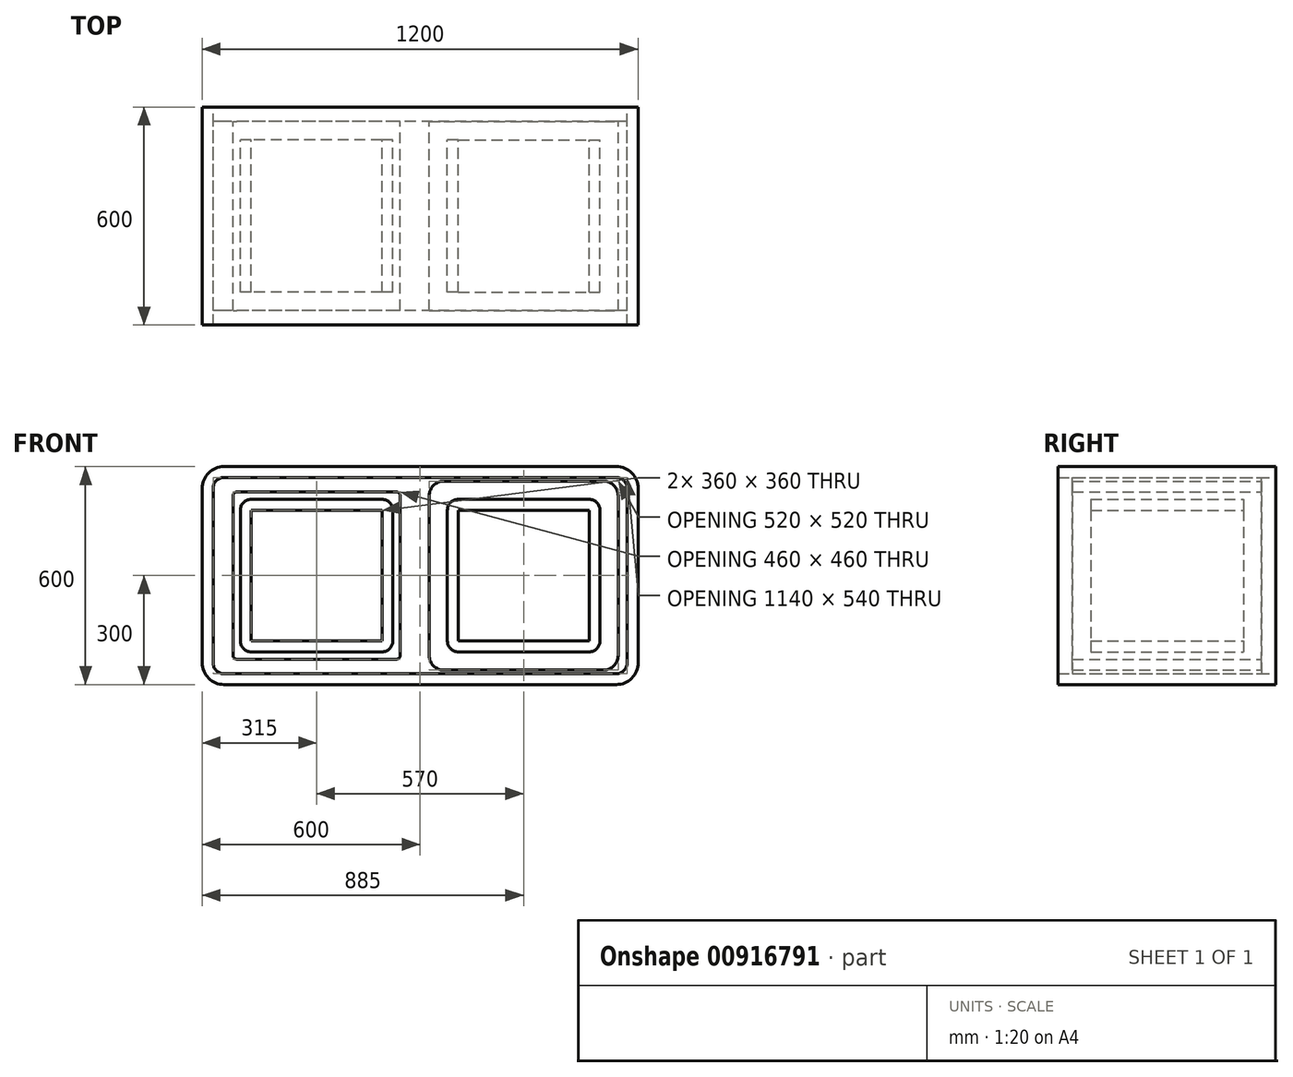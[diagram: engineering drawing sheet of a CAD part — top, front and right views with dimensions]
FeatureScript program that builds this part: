
annotation { "Feature Type Name" : "Feature", "Feature Type Description" : "" }
export const myFeature = defineFeature(function(context is Context, id is Id, definition is map)
    precondition{}
    {
        {
            var Q0;
            Q0=qCreatedBy(makeId("Front.planeOp"),FACE);
            var sketch = newSketch(context, id + "F0", { "sketchPlane" : qUnion([Q0])});
            skLineSegment(sketch, "E0.bottom", {"start": v(540, -300) * mm, "end": v(-540, -300) * mm});
            skLineSegment(sketch, "E0.top", {"start": v(540, 300) * mm, "end": v(-540, 300) * mm});
            skLineSegment(sketch, "E0.left", {"start": v(600, -240) * mm, "end": v(600, 240) * mm});
            skLineSegment(sketch, "E0.right", {"start": v(-600, -240) * mm, "end": v(-600, 240) * mm});
            skPoint(sketch, "E0.middle", {"position": v(0, 0) * mm});
            skPoint(sketch, "E1.visualSharp", {"position": v(-600, 300) * mm});
            skArc(sketch, "E1.filletArc", {"start": v(-540, 300) * mm, "mid": v(-582.43, 282.43) * mm, "end": v(-600, 240) * mm});
            skPoint(sketch, "E2.visualSharp", {"position": v(-600, -300) * mm});
            skArc(sketch, "E2.filletArc", {"start": v(-600, -240) * mm, "mid": v(-582.43, -282.43) * mm, "end": v(-540, -300) * mm});
            skPoint(sketch, "E3.visualSharp", {"position": v(600, -300) * mm});
            skArc(sketch, "E3.filletArc", {"start": v(540, -300) * mm, "mid": v(582.43, -282.43) * mm, "end": v(600, -240) * mm});
            skPoint(sketch, "E4.visualSharp", {"position": v(600, 300) * mm});
            skArc(sketch, "E4.filletArc", {"start": v(600, 240) * mm, "mid": v(582.43, 282.43) * mm, "end": v(540, 300) * mm});
            skArc(sketch, "E5.0", {"start": v(570, 240) * mm, "mid": v(561.21, 261.21) * mm, "end": v(540, 270) * mm});
            skLineSegment(sketch, "E5.1", {"start": v(570, -240) * mm, "end": v(570, 240) * mm});
            skLineSegment(sketch, "E5.2", {"start": v(540, 270) * mm, "end": v(-540, 270) * mm});
            skArc(sketch, "E5.3", {"start": v(540, -270) * mm, "mid": v(561.21, -261.21) * mm, "end": v(570, -240) * mm});
            skArc(sketch, "E5.4", {"start": v(-540, 270) * mm, "mid": v(-561.21, 261.21) * mm, "end": v(-570, 240) * mm});
            skLineSegment(sketch, "E5.5", {"start": v(-570, -240) * mm, "end": v(-570, 240) * mm});
            skArc(sketch, "E5.6", {"start": v(-570, -240) * mm, "mid": v(-561.21, -261.21) * mm, "end": v(-540, -270) * mm});
            skLineSegment(sketch, "E5.7", {"start": v(540, -270) * mm, "end": v(-540, -270) * mm});
            skLineSegment(sketch, "E6", {"start": v(0, 300) * mm, "end": v(0, -300) * mm, "construction": true});
            skLineSegment(sketch, "E7", {"start": v(0, 0) * mm, "end": v(-570, 0) * mm, "construction": true});
            skLineSegment(sketch, "E8.bottom", {"start": v(-65, 260) * mm, "end": v(-505, 260) * mm});
            skLineSegment(sketch, "E8.top", {"start": v(-65, -260) * mm, "end": v(-505, -260) * mm});
            skLineSegment(sketch, "E8.left", {"start": v(-25, 220) * mm, "end": v(-25, -220) * mm});
            skLineSegment(sketch, "E8.right", {"start": v(-545, 220) * mm, "end": v(-545, -220) * mm});
            skPoint(sketch, "E8.middle", {"position": v(-285, 0) * mm});
            skPoint(sketch, "E9.visualSharp", {"position": v(-25, 260) * mm});
            skArc(sketch, "E9.filletArc", {"start": v(-25, 220) * mm, "mid": v(-36.72, 248.28) * mm, "end": v(-65, 260) * mm});
            skPoint(sketch, "E10.visualSharp", {"position": v(-25, -260) * mm});
            skArc(sketch, "E10.filletArc", {"start": v(-65, -260) * mm, "mid": v(-36.72, -248.28) * mm, "end": v(-25, -220) * mm});
            skPoint(sketch, "E11.visualSharp", {"position": v(-545, -260) * mm});
            skArc(sketch, "E11.filletArc", {"start": v(-545, -220) * mm, "mid": v(-533.28, -248.28) * mm, "end": v(-505, -260) * mm});
            skPoint(sketch, "E12.visualSharp", {"position": v(-545, 260) * mm});
            skArc(sketch, "E12.filletArc", {"start": v(-505, 260) * mm, "mid": v(-533.28, 248.28) * mm, "end": v(-545, 220) * mm});
            skLineSegment(sketch, "E13.0", {"start": v(-55, 220) * mm, "end": v(-55, -220) * mm});
            skArc(sketch, "E13.1", {"start": v(-65, -230) * mm, "mid": v(-57.93, -227.07) * mm, "end": v(-55, -220) * mm});
            skArc(sketch, "E13.2", {"start": v(-55, 220) * mm, "mid": v(-57.93, 227.07) * mm, "end": v(-65, 230) * mm});
            skLineSegment(sketch, "E13.3", {"start": v(-65, -230) * mm, "end": v(-505, -230) * mm});
            skLineSegment(sketch, "E13.4", {"start": v(-65, 230) * mm, "end": v(-505, 230) * mm});
            skArc(sketch, "E13.5", {"start": v(-505, 230) * mm, "mid": v(-512.07, 227.07) * mm, "end": v(-515, 220) * mm});
            skLineSegment(sketch, "E13.6", {"start": v(-515, 220) * mm, "end": v(-515, -220) * mm});
            skArc(sketch, "E13.7", {"start": v(-515, -220) * mm, "mid": v(-512.07, -227.07) * mm, "end": v(-505, -230) * mm});
            skArc(sketch, "E14.MirrorCS", {"start": v(545, -220) * mm, "mid": v(533.28, -248.28) * mm, "end": v(505, -260) * mm});
            skArc(sketch, "E15.MirrorCS", {"start": v(515, -220) * mm, "mid": v(512.07, -227.07) * mm, "end": v(505, -230) * mm});
            skLineSegment(sketch, "E16.MirrorCS", {"start": v(65, -260) * mm, "end": v(505, -260) * mm});
            skLineSegment(sketch, "E17.MirrorCS", {"start": v(65, -230) * mm, "end": v(505, -230) * mm});
            skArc(sketch, "E18.MirrorCS", {"start": v(65, -230) * mm, "mid": v(57.93, -227.07) * mm, "end": v(55, -220) * mm});
            skArc(sketch, "E19.MirrorCS", {"start": v(65, -260) * mm, "mid": v(36.72, -248.28) * mm, "end": v(25, -220) * mm});
            skLineSegment(sketch, "E20.MirrorCS", {"start": v(55, 220) * mm, "end": v(55, -220) * mm});
            skArc(sketch, "E21.MirrorCS", {"start": v(55, 220) * mm, "mid": v(57.93, 227.07) * mm, "end": v(65, 230) * mm});
            skArc(sketch, "E22.MirrorCS", {"start": v(505, 230) * mm, "mid": v(512.07, 227.07) * mm, "end": v(515, 220) * mm});
            skLineSegment(sketch, "E23.MirrorCS", {"start": v(515, 220) * mm, "end": v(515, -220) * mm});
            skLineSegment(sketch, "E24.MirrorCS", {"start": v(545, 220) * mm, "end": v(545, -220) * mm});
            skLineSegment(sketch, "E25.MirrorCS", {"start": v(65, 230) * mm, "end": v(505, 230) * mm});
            skArc(sketch, "E26.MirrorCS", {"start": v(505, 260) * mm, "mid": v(533.28, 248.28) * mm, "end": v(545, 220) * mm});
            skLineSegment(sketch, "E27.MirrorCS", {"start": v(25, 220) * mm, "end": v(25, -220) * mm});
            skLineSegment(sketch, "E28.MirrorCS", {"start": v(65, 260) * mm, "end": v(505, 260) * mm});
            skArc(sketch, "E29.MirrorCS", {"start": v(25, 220) * mm, "mid": v(36.72, 248.28) * mm, "end": v(65, 260) * mm});
            skLineSegment(sketch, "E30.bottom", {"start": v(-105, 210) * mm, "end": v(-465, 210) * mm});
            skLineSegment(sketch, "E30.top", {"start": v(-105, -210) * mm, "end": v(-465, -210) * mm});
            skLineSegment(sketch, "E30.left", {"start": v(-75, 180) * mm, "end": v(-75, -180) * mm});
            skLineSegment(sketch, "E30.right", {"start": v(-495, 180) * mm, "end": v(-495, -180) * mm});
            skPoint(sketch, "E31.visualSharp", {"position": v(-495, 210) * mm});
            skArc(sketch, "E31.filletArc", {"start": v(-465, 210) * mm, "mid": v(-486.21, 201.21) * mm, "end": v(-495, 180) * mm});
            skPoint(sketch, "E32.visualSharp", {"position": v(-495, -210) * mm});
            skArc(sketch, "E32.filletArc", {"start": v(-495, -180) * mm, "mid": v(-486.21, -201.21) * mm, "end": v(-465, -210) * mm});
            skPoint(sketch, "E33.visualSharp", {"position": v(-75, -210) * mm});
            skArc(sketch, "E33.filletArc", {"start": v(-105, -210) * mm, "mid": v(-83.79, -201.21) * mm, "end": v(-75, -180) * mm});
            skPoint(sketch, "E34.visualSharp", {"position": v(-75, 210) * mm});
            skArc(sketch, "E34.filletArc", {"start": v(-75, 180) * mm, "mid": v(-83.79, 201.21) * mm, "end": v(-105, 210) * mm});
            skLineSegment(sketch, "E35.0", {"start": v(-465, 180) * mm, "end": v(-465, -180) * mm});
            skLineSegment(sketch, "E35.1", {"start": v(-105, 180) * mm, "end": v(-465, 180) * mm});
            skLineSegment(sketch, "E35.2", {"start": v(-105, 180) * mm, "end": v(-105, -180) * mm});
            skLineSegment(sketch, "E35.3", {"start": v(-105, -180) * mm, "end": v(-465, -180) * mm});
            skLineSegment(sketch, "E36.MirrorCS", {"start": v(105, -180) * mm, "end": v(465, -180) * mm});
            skLineSegment(sketch, "E37.MirrorCS", {"start": v(105, 180) * mm, "end": v(105, -180) * mm});
            skLineSegment(sketch, "E38.MirrorCS", {"start": v(105, 180) * mm, "end": v(465, 180) * mm});
            skLineSegment(sketch, "E39.MirrorCS", {"start": v(465, 180) * mm, "end": v(465, -180) * mm});
            skArc(sketch, "E40.MirrorCS", {"start": v(465, 210) * mm, "mid": v(486.21, 201.21) * mm, "end": v(495, 180) * mm});
            skLineSegment(sketch, "E41.MirrorCS", {"start": v(495, 180) * mm, "end": v(495, -180) * mm});
            skArc(sketch, "E42.MirrorCS", {"start": v(495, -180) * mm, "mid": v(486.21, -201.21) * mm, "end": v(465, -210) * mm});
            skLineSegment(sketch, "E43.MirrorCS", {"start": v(105, -210) * mm, "end": v(465, -210) * mm});
            skArc(sketch, "E44.MirrorCS", {"start": v(105, -210) * mm, "mid": v(83.79, -201.21) * mm, "end": v(75, -180) * mm});
            skLineSegment(sketch, "E45.MirrorCS", {"start": v(105, 210) * mm, "end": v(465, 210) * mm});
            skLineSegment(sketch, "E46.MirrorCS", {"start": v(75, 180) * mm, "end": v(75, -180) * mm});
            skArc(sketch, "E47.MirrorCS", {"start": v(75, 180) * mm, "mid": v(83.79, 201.21) * mm, "end": v(105, 210) * mm});
            skSolve(sketch);
        }
        {
            var Q0;
            Q0=qCreatedBy(makeId("Front.planeOp"),FACE);
            var sketch = newSketch(context, id + "F1", { "sketchPlane" : qUnion([Q0])});
            skLineSegment(sketch, "E48.0", {"start": v(540, 300) * mm, "end": v(-540, 300) * mm});
            skLineSegment(sketch, "E48.1", {"start": v(600, -240) * mm, "end": v(600, 240) * mm});
            skArc(sketch, "E48.2", {"start": v(600, 240) * mm, "mid": v(582.43, 282.43) * mm, "end": v(540, 300) * mm});
            skArc(sketch, "E48.3", {"start": v(540, -300) * mm, "mid": v(582.43, -282.43) * mm, "end": v(600, -240) * mm});
            skLineSegment(sketch, "E48.4", {"start": v(540, -300) * mm, "end": v(-540, -300) * mm});
            skLineSegment(sketch, "E48.5", {"start": v(-600, -240) * mm, "end": v(-600, 240) * mm});
            skArc(sketch, "E48.6", {"start": v(-600, -240) * mm, "mid": v(-582.43, -282.43) * mm, "end": v(-540, -300) * mm});
            skArc(sketch, "E48.7", {"start": v(-540, 300) * mm, "mid": v(-582.43, 282.43) * mm, "end": v(-600, 240) * mm});
            skArc(sketch, "E48.8", {"start": v(570, 240) * mm, "mid": v(561.21, 261.21) * mm, "end": v(540, 270) * mm});
            skLineSegment(sketch, "E48.9", {"start": v(570, -240) * mm, "end": v(570, 240) * mm});
            skLineSegment(sketch, "E48.10", {"start": v(540, 270) * mm, "end": v(-540, 270) * mm});
            skArc(sketch, "E48.11", {"start": v(540, -270) * mm, "mid": v(561.21, -261.21) * mm, "end": v(570, -240) * mm});
            skLineSegment(sketch, "E48.12", {"start": v(540, -270) * mm, "end": v(-540, -270) * mm});
            skArc(sketch, "E48.13", {"start": v(-570, -240) * mm, "mid": v(-561.21, -261.21) * mm, "end": v(-540, -270) * mm});
            skLineSegment(sketch, "E48.14", {"start": v(-570, -240) * mm, "end": v(-570, 240) * mm});
            skArc(sketch, "E48.15", {"start": v(-540, 270) * mm, "mid": v(-561.21, 261.21) * mm, "end": v(-570, 240) * mm});
            skPoint(sketch, "E48.16", {"position": v(-561.21, 261.21) * mm});
            skSolve(sketch);
        }
        {
            var Q0;
            Q0 = qSketchRegion(id + "F1", true);
            extrude(context, id + "F2", {"entities" : qUnion([Q0]), "endBound" : BoundingType.SYMMETRIC, "depth" : 600 * mm, "offsetDistance" : 25 * mm});
        }
        {
            var Q0;
            Q0=qCreatedBy(makeId("Front.planeOp"),FACE);
            var sketch = newSketch(context, id + "F3", { "sketchPlane" : qUnion([Q0])});
            skLineSegment(sketch, "E49.0", {"start": v(-65, 260) * mm, "end": v(-505, 260) * mm});
            skArc(sketch, "E49.1", {"start": v(-25, 220) * mm, "mid": v(-36.72, 248.28) * mm, "end": v(-65, 260) * mm});
            skLineSegment(sketch, "E49.2", {"start": v(-25, 220) * mm, "end": v(-25, -220) * mm});
            skArc(sketch, "E49.3", {"start": v(-65, -260) * mm, "mid": v(-36.72, -248.28) * mm, "end": v(-25, -220) * mm});
            skLineSegment(sketch, "E49.4", {"start": v(-65, -260) * mm, "end": v(-505, -260) * mm});
            skArc(sketch, "E49.5", {"start": v(-545, -220) * mm, "mid": v(-533.28, -248.28) * mm, "end": v(-505, -260) * mm});
            skLineSegment(sketch, "E49.6", {"start": v(-545, 220) * mm, "end": v(-545, -220) * mm});
            skArc(sketch, "E49.7", {"start": v(-505, 260) * mm, "mid": v(-533.28, 248.28) * mm, "end": v(-545, 220) * mm});
            skLineSegment(sketch, "E49.8", {"start": v(-65, 230) * mm, "end": v(-505, 230) * mm});
            skArc(sketch, "E49.9", {"start": v(-55, 220) * mm, "mid": v(-57.93, 227.07) * mm, "end": v(-65, 230) * mm});
            skLineSegment(sketch, "E49.10", {"start": v(-55, 220) * mm, "end": v(-55, -220) * mm});
            skArc(sketch, "E49.11", {"start": v(-65, -230) * mm, "mid": v(-57.93, -227.07) * mm, "end": v(-55, -220) * mm});
            skLineSegment(sketch, "E49.12", {"start": v(-65, -230) * mm, "end": v(-505, -230) * mm});
            skPoint(sketch, "E49.13", {"position": v(-505, -230) * mm});
            skLineSegment(sketch, "E49.14", {"start": v(-515, 220) * mm, "end": v(-515, -220) * mm});
            skArc(sketch, "E49.15", {"start": v(-515, -220) * mm, "mid": v(-512.07, -227.07) * mm, "end": v(-505, -230) * mm});
            skArc(sketch, "E49.16", {"start": v(-505, 230) * mm, "mid": v(-512.07, 227.07) * mm, "end": v(-515, 220) * mm});
            skArc(sketch, "E50.MirrorCS", {"start": v(515, -220) * mm, "mid": v(512.07, -227.07) * mm, "end": v(505, -230) * mm});
            skArc(sketch, "E51.MirrorCS", {"start": v(65, -230) * mm, "mid": v(57.93, -227.07) * mm, "end": v(55, -220) * mm});
            skArc(sketch, "E52.MirrorCS", {"start": v(55, 220) * mm, "mid": v(57.93, 227.07) * mm, "end": v(65, 230) * mm});
            skArc(sketch, "E53.MirrorCS", {"start": v(505, 230) * mm, "mid": v(512.07, 227.07) * mm, "end": v(515, 220) * mm});
            skLineSegment(sketch, "E54.MirrorCS", {"start": v(65, -230) * mm, "end": v(505, -230) * mm});
            skLineSegment(sketch, "E55.MirrorCS", {"start": v(55, 220) * mm, "end": v(55, -220) * mm});
            skLineSegment(sketch, "E56.MirrorCS", {"start": v(515, 220) * mm, "end": v(515, -220) * mm});
            skLineSegment(sketch, "E57.MirrorCS", {"start": v(65, 230) * mm, "end": v(505, 230) * mm});
            skArc(sketch, "E58.MirrorCS", {"start": v(505, 260) * mm, "mid": v(533.28, 248.28) * mm, "end": v(545, 220) * mm});
            skPoint(sketch, "E59.MirrorP", {"position": v(505, -230) * mm});
            skLineSegment(sketch, "E60.MirrorCS", {"start": v(545, 220) * mm, "end": v(545, -220) * mm});
            skArc(sketch, "E61.MirrorCS", {"start": v(545, -220) * mm, "mid": v(533.28, -248.28) * mm, "end": v(505, -260) * mm});
            skLineSegment(sketch, "E62.MirrorCS", {"start": v(65, -260) * mm, "end": v(505, -260) * mm});
            skArc(sketch, "E63.MirrorCS", {"start": v(65, -260) * mm, "mid": v(36.72, -248.28) * mm, "end": v(25, -220) * mm});
            skLineSegment(sketch, "E64.MirrorCS", {"start": v(65, 260) * mm, "end": v(505, 260) * mm});
            skLineSegment(sketch, "E65.MirrorCS", {"start": v(25, 220) * mm, "end": v(25, -220) * mm});
            skArc(sketch, "E66.MirrorCS", {"start": v(25, 220) * mm, "mid": v(36.72, 248.28) * mm, "end": v(65, 260) * mm});
            skSolve(sketch);
        }
        {
            var Q0;
            Q0 = qSketchRegion(id + "F3", true);
            var Q1;
            Q1=makeQuery(id+"F0.imprint","IMPRINT",FACE,{"disambiguationData":[TD([[makeQuery(id+"F0.imprint","IMPRINT",EDGE,{"derivedFrom":sQuery(id+"F0.wireOp",EDGE,"E14.MirrorCS")}),-1.0]])]});
            var Q2;
            Q2=makeQuery(id+"F0.imprint","IMPRINT",FACE,{"disambiguationData":[TD([[makeQuery(id+"F0.imprint","IMPRINT",EDGE,{"derivedFrom":sQuery(id+"F0.wireOp",EDGE,"E8.bottom")}),1.0]])]});
            extrude(context, id + "F4", {"entities" : qUnion([Q0, Q1, Q2]), "endBound" : BoundingType.SYMMETRIC, "depth" : 520 * mm, "offsetDistance" : 25 * mm});
        }
        {
            var Q0;
            Q0=makeQuery(id+"F4.opExtrude","SWEPT_BODY",BODY,{"disambiguationData":[OSD([sQuery(id+"F3.wireOp",EDGE,"E49.0"),sQuery(id+"F3.wireOp",EDGE,"E49.1"),sQuery(id+"F3.wireOp",EDGE,"E49.2"),sQuery(id+"F3.wireOp",EDGE,"E49.3"),sQuery(id+"F3.wireOp",EDGE,"E49.4"),sQuery(id+"F3.wireOp",EDGE,"E49.5"),sQuery(id+"F3.wireOp",EDGE,"E49.6"),sQuery(id+"F3.wireOp",EDGE,"E49.7"),sQuery(id+"F3.wireOp",EDGE,"E49.8"),sQuery(id+"F3.wireOp",EDGE,"E49.9"),sQuery(id+"F3.wireOp",EDGE,"E49.10"),sQuery(id+"F3.wireOp",EDGE,"E49.11"),sQuery(id+"F3.wireOp",EDGE,"E49.12"),sQuery(id+"F3.wireOp",EDGE,"E49.14"),sQuery(id+"F3.wireOp",EDGE,"E49.15"),sQuery(id+"F3.wireOp",EDGE,"E49.16")])]});
            var Q1;
            Q1=makeQuery(id+"F4.opExtrude","SWEPT_BODY",BODY,{"disambiguationData":[OSD([sQuery(id+"F3.wireOp",EDGE,"E50.MirrorCS"),sQuery(id+"F3.wireOp",EDGE,"E51.MirrorCS"),sQuery(id+"F3.wireOp",EDGE,"E52.MirrorCS"),sQuery(id+"F3.wireOp",EDGE,"E53.MirrorCS"),sQuery(id+"F3.wireOp",EDGE,"E54.MirrorCS"),sQuery(id+"F3.wireOp",EDGE,"E55.MirrorCS"),sQuery(id+"F3.wireOp",EDGE,"E56.MirrorCS"),sQuery(id+"F3.wireOp",EDGE,"E57.MirrorCS"),sQuery(id+"F3.wireOp",EDGE,"E58.MirrorCS"),sQuery(id+"F3.wireOp",EDGE,"E60.MirrorCS"),sQuery(id+"F3.wireOp",EDGE,"E61.MirrorCS"),sQuery(id+"F3.wireOp",EDGE,"E62.MirrorCS"),sQuery(id+"F3.wireOp",EDGE,"E63.MirrorCS"),sQuery(id+"F3.wireOp",EDGE,"E64.MirrorCS"),sQuery(id+"F3.wireOp",EDGE,"E65.MirrorCS"),sQuery(id+"F3.wireOp",EDGE,"E66.MirrorCS")])]});
            deleteBodies(context, id + "F5", {"entities" : qUnion([Q0, Q1])});
        }
        {
            var Q0;
            Q0=qCreatedBy(makeId("Front.planeOp"),FACE);
            var sketch = newSketch(context, id + "F6", { "sketchPlane" : qUnion([Q0])});
            skLineSegment(sketch, "E67.0", {"start": v(-105, 210) * mm, "end": v(-465, 210) * mm});
            skPoint(sketch, "E67.1", {"position": v(-465, 210) * mm});
            skArc(sketch, "E67.2", {"start": v(-465, 210) * mm, "mid": v(-486.21, 201.21) * mm, "end": v(-495, 180) * mm});
            skLineSegment(sketch, "E67.3", {"start": v(-495, 180) * mm, "end": v(-495, -180) * mm});
            skPoint(sketch, "E67.4", {"position": v(-465, -210) * mm});
            skLineSegment(sketch, "E67.5", {"start": v(-105, -210) * mm, "end": v(-465, -210) * mm});
            skLineSegment(sketch, "E67.6", {"start": v(-75, 180) * mm, "end": v(-75, -180) * mm});
            skArc(sketch, "E67.7", {"start": v(-75, 180) * mm, "mid": v(-83.79, 201.21) * mm, "end": v(-105, 210) * mm});
            skLineSegment(sketch, "E67.8", {"start": v(105, 210) * mm, "end": v(465, 210) * mm});
            skArc(sketch, "E67.9", {"start": v(75, 180) * mm, "mid": v(83.79, 201.21) * mm, "end": v(105, 210) * mm});
            skLineSegment(sketch, "E67.10", {"start": v(75, 180) * mm, "end": v(75, -180) * mm});
            skLineSegment(sketch, "E67.11", {"start": v(105, 180) * mm, "end": v(105, -180) * mm});
            skLineSegment(sketch, "E67.12", {"start": v(105, 180) * mm, "end": v(465, 180) * mm});
            skLineSegment(sketch, "E67.13", {"start": v(-105, 180) * mm, "end": v(-105, -180) * mm});
            skLineSegment(sketch, "E67.14", {"start": v(-105, 180) * mm, "end": v(-465, 180) * mm});
            skLineSegment(sketch, "E67.15", {"start": v(-465, 180) * mm, "end": v(-465, -180) * mm});
            skArc(sketch, "E67.16", {"start": v(465, 210) * mm, "mid": v(486.21, 201.21) * mm, "end": v(495, 180) * mm});
            skLineSegment(sketch, "E67.17", {"start": v(465, 180) * mm, "end": v(465, -180) * mm});
            skLineSegment(sketch, "E67.18", {"start": v(495, 180) * mm, "end": v(495, -180) * mm});
            skArc(sketch, "E67.19", {"start": v(495, -180) * mm, "mid": v(486.21, -201.21) * mm, "end": v(465, -210) * mm});
            skLineSegment(sketch, "E67.20", {"start": v(105, -180) * mm, "end": v(465, -180) * mm});
            skLineSegment(sketch, "E67.21", {"start": v(105, -210) * mm, "end": v(465, -210) * mm});
            skArc(sketch, "E67.22", {"start": v(105, -210) * mm, "mid": v(83.79, -201.21) * mm, "end": v(75, -180) * mm});
            skArc(sketch, "E67.23", {"start": v(-105, -210) * mm, "mid": v(-83.79, -201.21) * mm, "end": v(-75, -180) * mm});
            skLineSegment(sketch, "E67.24", {"start": v(-105, -180) * mm, "end": v(-465, -180) * mm});
            skArc(sketch, "E67.25", {"start": v(-495, -180) * mm, "mid": v(-486.21, -201.21) * mm, "end": v(-465, -210) * mm});
            skPoint(sketch, "E67.26", {"position": v(-486.21, -201.21) * mm});
            skPoint(sketch, "E67.27", {"position": v(-83.79, 201.21) * mm});
            skPoint(sketch, "E67.28", {"position": v(-83.79, -201.21) * mm});
            skPoint(sketch, "E67.29", {"position": v(83.79, -201.21) * mm});
            skSolve(sketch);
        }
        {
            var Q0;
            Q0 = qSketchRegion(id + "F6", true);
            extrude(context, id + "F7", {"entities" : qUnion([Q0]), "endBound" : BoundingType.SYMMETRIC, "depth" : 420 * mm, "offsetDistance" : 25 * mm});
        }
    });
